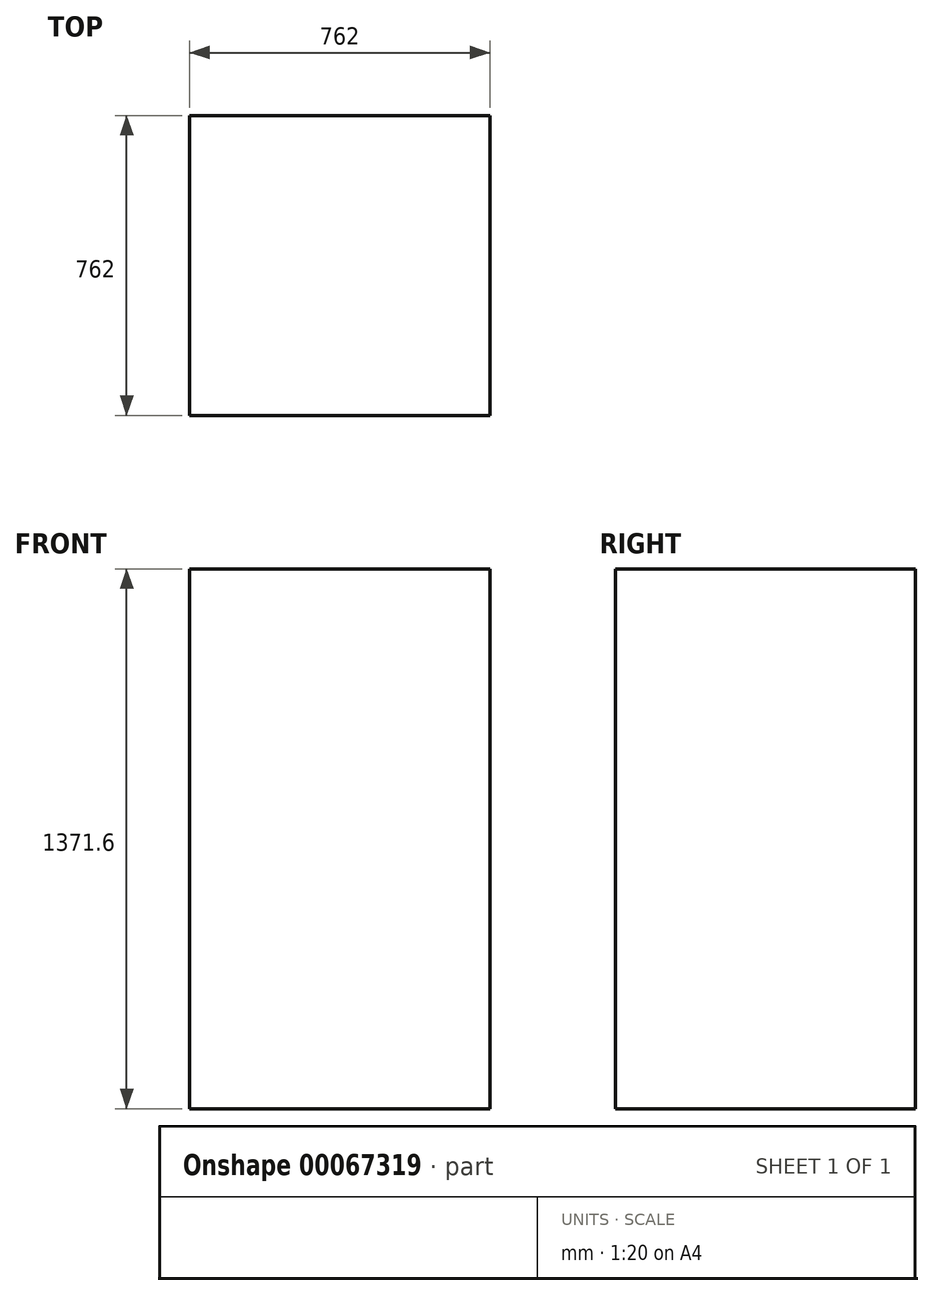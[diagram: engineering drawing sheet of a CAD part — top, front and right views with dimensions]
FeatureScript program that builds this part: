
annotation { "Feature Type Name" : "Feature", "Feature Type Description" : "" }
export const myFeature = defineFeature(function(context is Context, id is Id, definition is map)
    precondition{}
    {
        {
            var Q0;
            Q0=qCreatedBy(makeId("Top.planeOp"),FACE);
            var sketch = newSketch(context, id + "F0", { "sketchPlane" : qUnion([Q0])});
            skLineSegment(sketch, "E0.bottom", {"start": v(-362.21, 516.68) * mm, "end": v(399.79, 516.68) * mm});
            skLineSegment(sketch, "E0.top", {"start": v(-362.21, -245.32) * mm, "end": v(399.79, -245.32) * mm});
            skLineSegment(sketch, "E0.left", {"start": v(-362.21, 516.68) * mm, "end": v(-362.21, -245.32) * mm});
            skLineSegment(sketch, "E0.right", {"start": v(399.79, 516.68) * mm, "end": v(399.79, -245.32) * mm});
            skSolve(sketch);
        }
        {
            var Q0;
            Q0=makeQuery(id+"F0.imprint","IMPRINT",FACE,{"disambiguationData":[TD([[makeQuery(id+"F0.imprint","IMPRINT",EDGE,{"derivedFrom":sQuery(id+"F0.wireOp",EDGE,"E0.bottom")}),-1.0]])]});
            extrude(context, id + "F1", {"entities" : qUnion([Q0]), "depth" : 1371.6 * mm});
        }
    });
